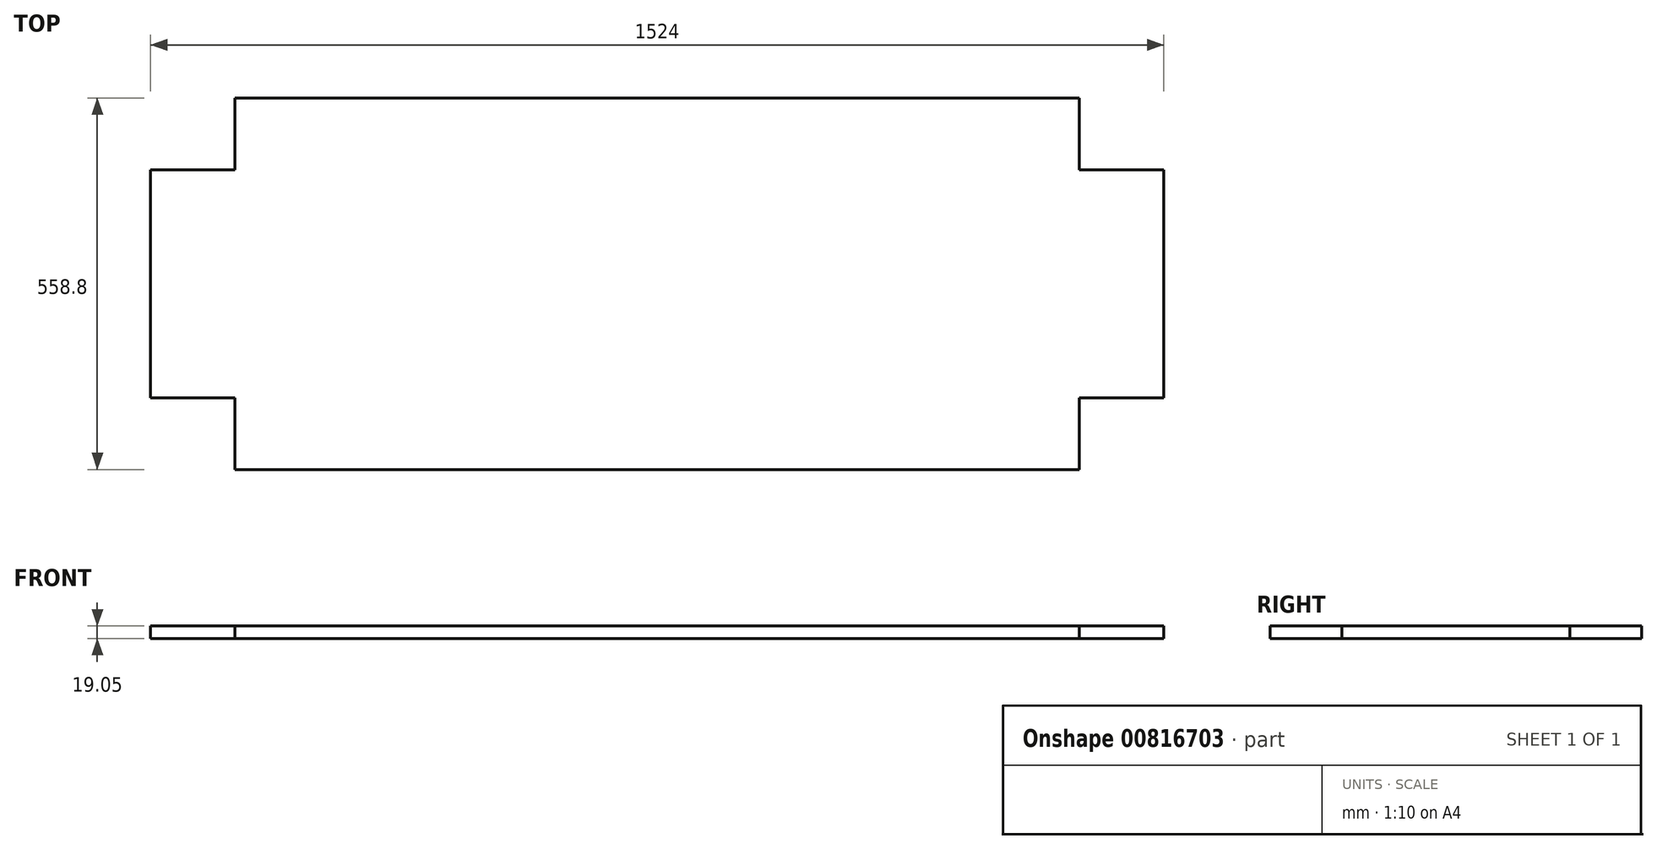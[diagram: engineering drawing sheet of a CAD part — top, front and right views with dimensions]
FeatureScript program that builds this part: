
annotation { "Feature Type Name" : "Feature", "Feature Type Description" : "" }
export const myFeature = defineFeature(function(context is Context, id is Id, definition is map)
    precondition{}
    {
        {
            var Q0;
            Q0=qCreatedBy(makeId("Top.planeOp"),FACE);
            var sketch = newSketch(context, id + "F0", { "sketchPlane" : qUnion([Q0])});
            skLineSegment(sketch, "E0", {"start": v(0, 0) * mm, "end": v(0, 107.95) * mm});
            skLineSegment(sketch, "E1", {"start": v(0, 107.95) * mm, "end": v(-127, 107.95) * mm});
            skLineSegment(sketch, "E2", {"start": v(-127, 107.95) * mm, "end": v(-127, 450.85) * mm});
            skLineSegment(sketch, "E3", {"start": v(-127, 450.85) * mm, "end": v(0, 450.85) * mm});
            skLineSegment(sketch, "E4", {"start": v(0, 450.85) * mm, "end": v(0, 558.8) * mm});
            skLineSegment(sketch, "E5", {"start": v(0, 558.8) * mm, "end": v(1270, 558.8) * mm});
            skLineSegment(sketch, "E6", {"start": v(1270, 558.8) * mm, "end": v(1270, 450.85) * mm});
            skLineSegment(sketch, "E7", {"start": v(1270, 450.85) * mm, "end": v(1397, 450.85) * mm});
            skLineSegment(sketch, "E8", {"start": v(1397, 450.85) * mm, "end": v(1397, 107.95) * mm});
            skLineSegment(sketch, "E9", {"start": v(1397, 107.95) * mm, "end": v(1270, 107.95) * mm});
            skLineSegment(sketch, "E10", {"start": v(1270, 107.95) * mm, "end": v(1270, 0) * mm});
            skLineSegment(sketch, "E11", {"start": v(1270, 0) * mm, "end": v(0, 0) * mm});
            skSolve(sketch);
        }
        {
            var Q0;
            Q0 = qSketchRegion(id + "F0", true);
            extrude(context, id + "F1", {"entities" : qUnion([Q0]), "depth" : 19.05 * mm, "offsetDistance" : 25.4 * mm});
        }
    });
